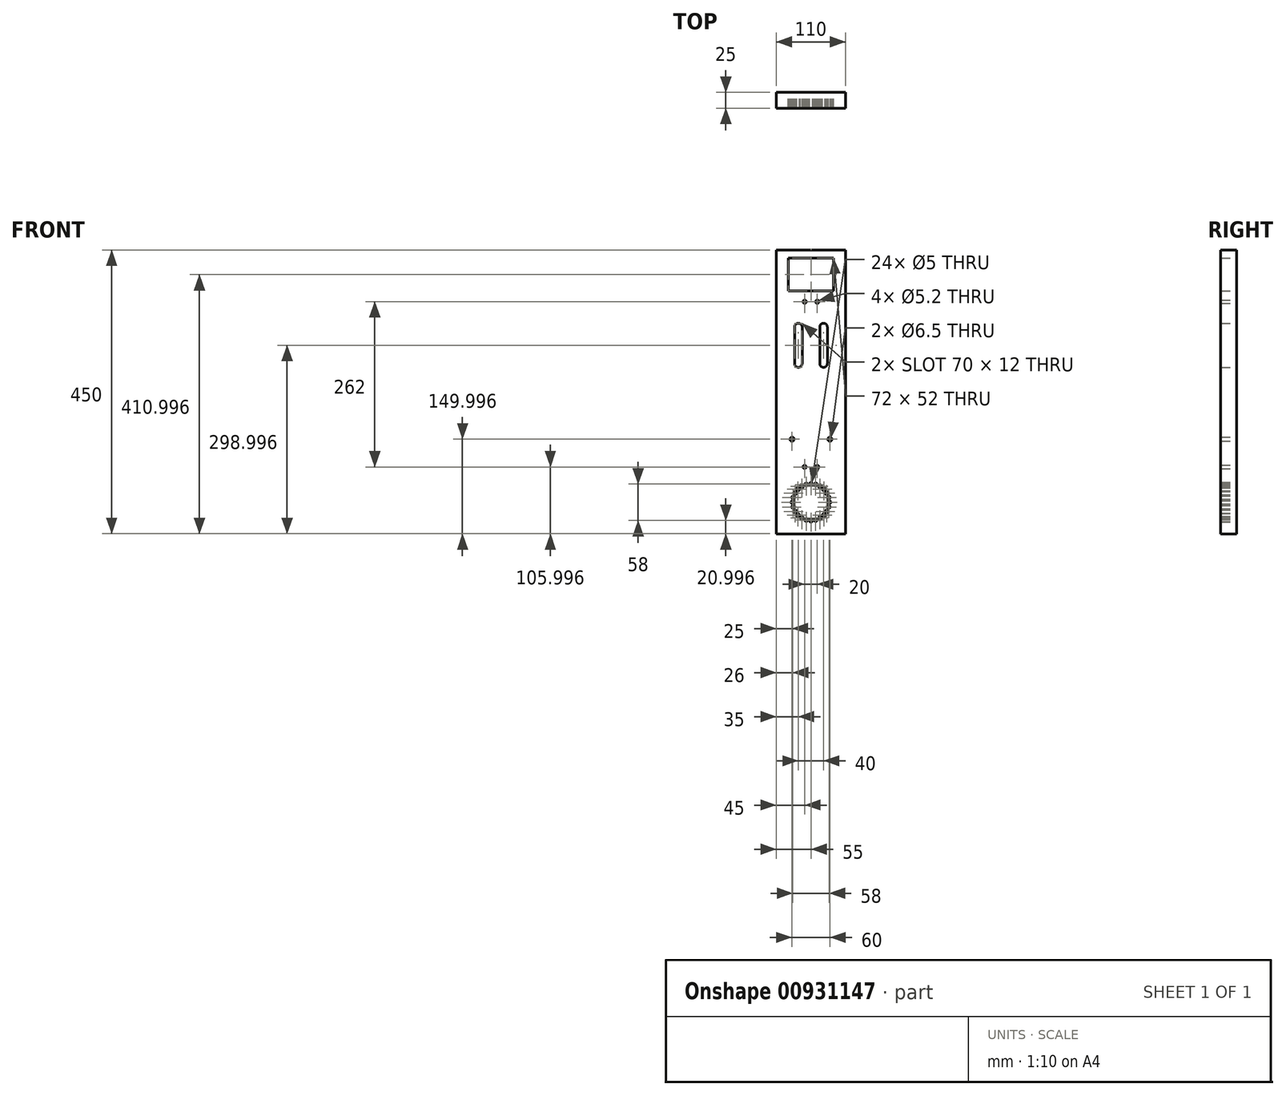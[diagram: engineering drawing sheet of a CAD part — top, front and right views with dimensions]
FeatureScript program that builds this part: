
annotation { "Feature Type Name" : "Feature", "Feature Type Description" : "" }
export const myFeature = defineFeature(function(context is Context, id is Id, definition is map)
    precondition{}
    {
        {
            var Q0;
            Q0=qCreatedBy(makeId("Front.planeOp"),FACE);
            var sketch = newSketch(context, id + "F0", { "sketchPlane" : qUnion([Q0])});
            skLineSegment(sketch, "E0.bottom", {"start": v(-55, 411.1) * mm, "end": v(55, 411.1) * mm});
            skLineSegment(sketch, "E0.top", {"start": v(-55, -38.9) * mm, "end": v(55, -38.9) * mm});
            skLineSegment(sketch, "E0.left", {"start": v(-55, 411.1) * mm, "end": v(-55, -38.9) * mm});
            skLineSegment(sketch, "E0.right", {"start": v(55, 411.1) * mm, "end": v(55, -38.9) * mm});
            skLineSegment(sketch, "E1.bottom", {"start": v(-36, 398.1) * mm, "end": v(36, 398.1) * mm});
            skLineSegment(sketch, "E1.top", {"start": v(-36, 346.1) * mm, "end": v(36, 346.1) * mm});
            skLineSegment(sketch, "E1.left", {"start": v(-36, 398.1) * mm, "end": v(-36, 346.1) * mm});
            skLineSegment(sketch, "E1.right", {"start": v(36, 398.1) * mm, "end": v(36, 346.1) * mm});
            skCircle(sketch, "E2", {"center": v(-10, 329.1) * mm, "radius": 2.6 * mm});
            skCircle(sketch, "E3", {"center": v(10, 329.1) * mm, "radius": 2.6 * mm});
            skCircle(sketch, "E4", {"center": v(-10, 67.1) * mm, "radius": 2.6 * mm});
            skCircle(sketch, "E5", {"center": v(10, 67.1) * mm, "radius": 2.6 * mm});
            skLineSegment(sketch, "E6.bottom", {"start": v(-20, 295.1) * mm, "end": v(-20, 295.1) * mm});
            skLineSegment(sketch, "E6.top", {"start": v(-20, 225.1) * mm, "end": v(-20, 225.1) * mm});
            skLineSegment(sketch, "E6.left", {"start": v(-26, 289.1) * mm, "end": v(-26, 231.1) * mm});
            skLineSegment(sketch, "E6.right", {"start": v(-14, 289.1) * mm, "end": v(-14, 231.1) * mm});
            skPoint(sketch, "E7.visualSharp", {"position": v(-14, 295.1) * mm});
            skArc(sketch, "E7.filletArc", {"start": v(-14, 289.1) * mm, "mid": v(-15.76, 293.34) * mm, "end": v(-20, 295.1) * mm});
            skPoint(sketch, "E8.visualSharp", {"position": v(-26, 295.1) * mm});
            skArc(sketch, "E8.filletArc", {"start": v(-20, 295.1) * mm, "mid": v(-24.24, 293.34) * mm, "end": v(-26, 289.1) * mm});
            skPoint(sketch, "E9.visualSharp", {"position": v(-26, 225.1) * mm});
            skArc(sketch, "E9.filletArc", {"start": v(-26, 231.1) * mm, "mid": v(-24.24, 226.85) * mm, "end": v(-20, 225.1) * mm});
            skPoint(sketch, "E10.visualSharp", {"position": v(-14, 225.1) * mm});
            skArc(sketch, "E10.filletArc", {"start": v(-20, 225.1) * mm, "mid": v(-15.76, 226.85) * mm, "end": v(-14, 231.1) * mm});
            skLineSegment(sketch, "E11.bottom", {"start": v(20, 295.1) * mm, "end": v(20, 295.1) * mm});
            skLineSegment(sketch, "E11.top", {"start": v(20, 225.1) * mm, "end": v(20, 225.1) * mm});
            skLineSegment(sketch, "E11.left", {"start": v(14, 289.1) * mm, "end": v(14, 231.1) * mm});
            skLineSegment(sketch, "E11.right", {"start": v(26, 289.1) * mm, "end": v(26, 231.1) * mm});
            skPoint(sketch, "E12.visualSharp", {"position": v(26, 295.1) * mm});
            skArc(sketch, "E12.filletArc", {"start": v(26, 289.1) * mm, "mid": v(24.24, 293.34) * mm, "end": v(20, 295.1) * mm});
            skPoint(sketch, "E13.visualSharp", {"position": v(14, 295.1) * mm});
            skArc(sketch, "E13.filletArc", {"start": v(20, 295.1) * mm, "mid": v(15.76, 293.34) * mm, "end": v(14, 289.1) * mm});
            skPoint(sketch, "E14.visualSharp", {"position": v(14, 225.1) * mm});
            skArc(sketch, "E14.filletArc", {"start": v(14, 231.1) * mm, "mid": v(15.76, 226.85) * mm, "end": v(20, 225.1) * mm});
            skPoint(sketch, "E15.visualSharp", {"position": v(26, 225.1) * mm});
            skArc(sketch, "E15.filletArc", {"start": v(20, 225.1) * mm, "mid": v(24.24, 226.85) * mm, "end": v(26, 231.1) * mm});
            skCircle(sketch, "E16", {"center": v(0, 40.1) * mm, "radius": 2.5 * mm});
            skCircle(sketch, "E17.1.0", {"center": v(-7.5, 39.1) * mm, "radius": 2.5 * mm});
            skCircle(sketch, "E17.2.0", {"center": v(-14.5, 36.21) * mm, "radius": 2.5 * mm});
            skPoint(sketch, "E17.center", {"position": v(0, 11.1) * mm});
            skCircle(sketch, "E18.1.3.0", {"center": v(-20.5, 31.6) * mm, "radius": 2.5 * mm});
            skCircle(sketch, "E18.1.4.0", {"center": v(-25.11, 25.6) * mm, "radius": 2.5 * mm});
            skCircle(sketch, "E18.1.5.0", {"center": v(-28.01, 18.6) * mm, "radius": 2.5 * mm});
            skCircle(sketch, "E18.1.6.0", {"center": v(-29, 11.1) * mm, "radius": 2.5 * mm});
            skCircle(sketch, "E18.1.7.0", {"center": v(-28.01, 3.59) * mm, "radius": 2.5 * mm});
            skCircle(sketch, "E18.1.8.0", {"center": v(-25.11, -3.4) * mm, "radius": 2.5 * mm});
            skCircle(sketch, "E18.1.9.0", {"center": v(-20.5, -9.41) * mm, "radius": 2.5 * mm});
            skCircle(sketch, "E19.1.10.0", {"center": v(-14.5, -14.02) * mm, "radius": 2.5 * mm});
            skCircle(sketch, "E19.1.11.0", {"center": v(-7.5, -16.92) * mm, "radius": 2.5 * mm});
            skCircle(sketch, "E19.1.12.0", {"center": v(0, -17.9) * mm, "radius": 2.5 * mm});
            skCircle(sketch, "E19.1.13.0", {"center": v(7.5, -16.92) * mm, "radius": 2.5 * mm});
            skCircle(sketch, "E19.1.14.0", {"center": v(14.5, -14.02) * mm, "radius": 2.5 * mm});
            skCircle(sketch, "E19.1.15.0", {"center": v(20.5, -9.41) * mm, "radius": 2.5 * mm});
            skCircle(sketch, "E19.1.16.0", {"center": v(25.11, -3.4) * mm, "radius": 2.5 * mm});
            skCircle(sketch, "E19.1.17.0", {"center": v(28.01, 3.59) * mm, "radius": 2.5 * mm});
            skCircle(sketch, "E19.1.18.0", {"center": v(29, 11.1) * mm, "radius": 2.5 * mm});
            skCircle(sketch, "E19.1.19.0", {"center": v(28.01, 18.6) * mm, "radius": 2.5 * mm});
            skCircle(sketch, "E19.1.20.0", {"center": v(25.11, 25.6) * mm, "radius": 2.5 * mm});
            skCircle(sketch, "E19.1.21.0", {"center": v(20.5, 31.6) * mm, "radius": 2.5 * mm});
            skCircle(sketch, "E19.1.22.0", {"center": v(14.5, 36.21) * mm, "radius": 2.5 * mm});
            skCircle(sketch, "E19.1.23.0", {"center": v(7.5, 39.1) * mm, "radius": 2.5 * mm});
            skPoint(sketch, "E20.center", {"position": v(0, 0) * mm});
            skCircle(sketch, "E21", {"center": v(-30, 111.1) * mm, "radius": 3.25 * mm});
            skCircle(sketch, "E22", {"center": v(30, 111.1) * mm, "radius": 3.25 * mm});
            skSolve(sketch);
        }
        {
            var Q0;
            Q0=makeQuery(id+"F0.imprint","IMPRINT",FACE,{"disambiguationData":[TD([[makeQuery(id+"F0.imprint","IMPRINT",EDGE,{"derivedFrom":sQuery(id+"F0.wireOp",EDGE,"E0.bottom")}),-1.0]])]});
            extrude(context, id + "F1", {"entities" : qUnion([Q0]), "depth" : 25 * mm, "offsetDistance" : 25 * mm});
        }
    });
